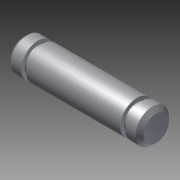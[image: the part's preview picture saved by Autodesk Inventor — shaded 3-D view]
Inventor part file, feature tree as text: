
AUTODESK INVENTOR PART (.ipt)
format: ipt  version: 2012 (Build 160160000, 160)  size: 133,120 bytes
history: native  units: in
note: dims shown in document units (in); Inventor stores cm internally (conversion verified against a paired STEP export)
features: other x49, revolve x1, sketch x1
ambient origin geometry x8: Origin, YZ Plane, XZ Plane, XY Plane, X Axis, Y Axis, Z Axis, Center Point
bodies: Solid1 (feature_tree)
feature tree (51):
  revolve  "Revolution1"  [1 undecoded]
  other  "pin_XY"
  other  "pin_YZ"
  other  "pin_ZX"
  other  "pin_X"
  other  "pin_Y"
  other  "pin_Z"
  other  "pin_Center"
  other  "rr1_XY"
  other  "rr1_YZ"
  other  "rr1_ZX"
  other  "rr1_X"
  other  "rr1_Y"
  other  "rr1_Z"
  other  "rr1_Center"
  other  "rr2_XY"
  other  "rr2_YZ"
  other  "rr2_ZX"
  other  "rr2_X"
  other  "rr2_Y"
  other  "rr2_Z"
  other  "rr2_Center"
  other  "w21_XY"
  other  "w21_YZ"
  other  "w21_ZX"
  other  "w21_X"
  other  "w21_Y"
  other  "w21_Z"
  other  "w21_Center"
  other  "w22_XY"
  other  "w22_YZ"
  other  "w22_ZX"
  other  "w22_X"
  other  "w22_Y"
  other  "w22_Z"
  other  "w22_Center"
  other  "p1_XY"
  other  "p1_YZ"
  other  "p1_ZX"
  other  "p1_X"
  other  "p1_Y"
  other  "p1_Z"
  other  "p1_Center"
  other  "p2_XY"
  other  "p2_YZ"
  other  "p2_ZX"
  other  "p2_X"
  other  "p2_Y"
  other  "p2_Z"
  other  "p2_Center"
  sketch  "Sketch_1"  dims[d0=360.0deg]
note: 1 required parameter value undecoded (feature->parameter linkage not recoverable at this tier; creation-order binding heuristic only, values carry confidence <= 0.55)
